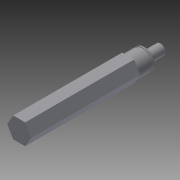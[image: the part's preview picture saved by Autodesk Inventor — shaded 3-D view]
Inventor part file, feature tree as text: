
AUTODESK INVENTOR PART (.ipt)
format: ipt  version: 2015 SP1 (Build 190203100, 203)  size: 108,032 bytes
history: native  units: in
note: dims shown in document units (in); Inventor stores cm internally (conversion verified against a paired STEP export)
features: chamfer x1, other x1, extrude x1, imported_body x1, sketch x1
ambient origin geometry x8: Origin, YZ Plane, XZ Plane, XY Plane, X Axis, Y Axis, Z Axis, Center Point
bodies: Body1 (feature_tree)
feature tree (5):
  chamfer  "Chamfer1"  Distance=2.0in
  other  "DriveShaft.ipt1"
  extrude  "Extrusion1"  [1 undecoded]
  imported_body  "Base1"
  sketch  "Sketch1"  dims[d0=0.75in d1=2.0in d2=0.0in]
note: 1 required parameter value undecoded (feature->parameter linkage not recoverable at this tier; creation-order binding heuristic only, values carry confidence <= 0.55)
